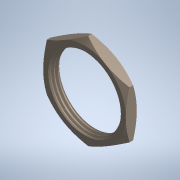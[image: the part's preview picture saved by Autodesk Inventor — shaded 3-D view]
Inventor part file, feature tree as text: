
AUTODESK INVENTOR PART (.ipt)
format: ipt  version: 2022 (Build 260153000, 153)  size: 245,760 bytes
history: imported  units: mm (DEFAULTED — no unit token found)
features: other x10, sketch x1, imported_body x1
bodies: Body1 (imported_parasolid)
feature tree (12):
  other  "Sólido1"
  other  "Origen"
  other  "Geometría reparada1"
  other  "Plano YZ"
  other  "Plano XZ"
  other  "Plano XY"
  other  "Eje X"
  other  "Eje Y"
  other  "Eje Z"
  sketch  "Boceto 3D1"
  other  "Cortar-Barrer1"
  imported_body  NMx_Import_Brep_tag  [imported B-rep: ~6 faces, bbox_mm=None]
